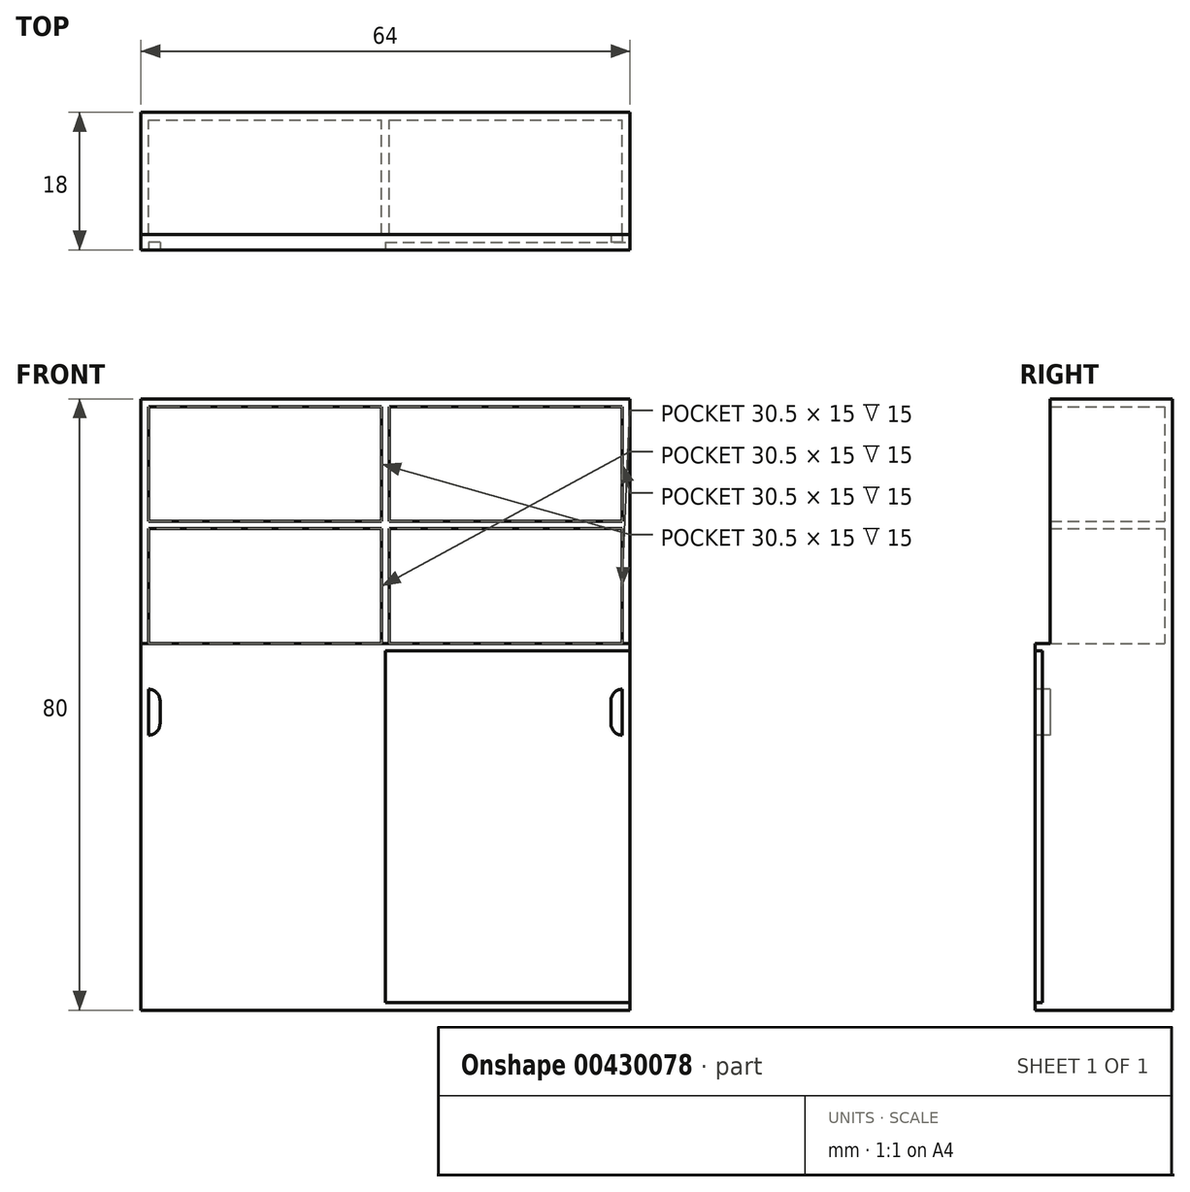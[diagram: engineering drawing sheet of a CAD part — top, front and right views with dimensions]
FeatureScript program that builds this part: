
annotation { "Feature Type Name" : "Feature", "Feature Type Description" : "" }
export const myFeature = defineFeature(function(context is Context, id is Id, definition is map)
    precondition{}
    {
        {
            var Q0;
            Q0=qCreatedBy(makeId("Top.planeOp"),FACE);
            var sketch = newSketch(context, id + "F0", { "sketchPlane" : qUnion([Q0])});
            skLineSegment(sketch, "E0.bottom", {"start": v(0, 0) * mm, "end": v(64, 0) * mm});
            skLineSegment(sketch, "E0.top", {"start": v(0, 18) * mm, "end": v(64, 18) * mm});
            skLineSegment(sketch, "E0.left", {"start": v(0, 0) * mm, "end": v(0, 18) * mm});
            skLineSegment(sketch, "E0.right", {"start": v(64, 0) * mm, "end": v(64, 18) * mm});
            skSolve(sketch);
        }
        {
            var Q0;
            Q0=makeQuery(id+"F0.imprint","IMPRINT",FACE,{"disambiguationData":[TD([[makeQuery(id+"F0.imprint","IMPRINT",EDGE,{"derivedFrom":sQuery(id+"F0.wireOp",EDGE,"E0.bottom")}),1.0]])]});
            extrude(context, id + "F1", {"entities" : qUnion([Q0]), "depth" : 48 * mm});
        }
        {
            var Q0;
            Q0=makeQuery(id+"F1.opExtrude","CAP_FACE",FACE,{"disambiguationData":[OSD([sQuery(id+"F0.wireOp",EDGE,"E0.bottom"),sQuery(id+"F0.wireOp",EDGE,"E0.top"),sQuery(id+"F0.wireOp",EDGE,"E0.left"),sQuery(id+"F0.wireOp",EDGE,"E0.right")])],"isStart":false});
            var sketch = newSketch(context, id + "F2", { "sketchPlane" : qUnion([Q0])});
            skLineSegment(sketch, "E1.bottom", {"start": v(0, 18) * mm, "end": v(64, 18) * mm});
            skLineSegment(sketch, "E1.top", {"start": v(0, 17) * mm, "end": v(64, 17) * mm});
            skLineSegment(sketch, "E1.left", {"start": v(0, 18) * mm, "end": v(0, 17) * mm});
            skLineSegment(sketch, "E1.right", {"start": v(64, 18) * mm, "end": v(64, 17) * mm});
            skSolve(sketch);
        }
        {
            var Q0;
            Q0=makeQuery(id+"F2.imprint","IMPRINT",FACE,{"disambiguationData":[TD([[makeQuery(id+"F2.imprint","IMPRINT",EDGE,{"derivedFrom":sQuery(id+"F2.wireOp",EDGE,"E1.bottom")}),-1.0]])]});
            extrude(context, id + "F3", {"entities" : qUnion([Q0]), "operationType" : NewBodyOperationType.ADD, "depth" : 32 * mm});
        }
        {
            var Q0;
            Q0=makeQuery(id+"F3.opExtrude","SWEPT_FACE",FACE,{"disambiguationData":[OSD([sQuery(id+"F2.wireOp",EDGE,"E1.top")])]});
            var sketch = newSketch(context, id + "F4", { "sketchPlane" : qUnion([Q0])});
            skLineSegment(sketch, "E2.bottom", {"start": v(0, 80) * mm, "end": v(1, 80) * mm});
            skLineSegment(sketch, "E2.top", {"start": v(0, 48) * mm, "end": v(1, 48) * mm});
            skLineSegment(sketch, "E2.left", {"start": v(0, 80) * mm, "end": v(0, 48) * mm});
            skLineSegment(sketch, "E2.right", {"start": v(1, 79) * mm, "end": v(1, 64) * mm});
            skLineSegment(sketch, "E3.bottom", {"start": v(63, 80) * mm, "end": v(64, 80) * mm});
            skLineSegment(sketch, "E3.top", {"start": v(63, 48) * mm, "end": v(64, 48) * mm});
            skLineSegment(sketch, "E3.left", {"start": v(63, 79) * mm, "end": v(63, 64) * mm});
            skLineSegment(sketch, "E3.right", {"start": v(64, 80) * mm, "end": v(64, 48) * mm});
            skLineSegment(sketch, "E4.bottom", {"start": v(31.5, 80) * mm, "end": v(32.5, 80) * mm});
            skLineSegment(sketch, "E4.top", {"start": v(31.5, 48) * mm, "end": v(32.5, 48) * mm});
            skLineSegment(sketch, "E4.left", {"start": v(31.5, 79) * mm, "end": v(31.5, 64) * mm});
            skLineSegment(sketch, "E4.right", {"start": v(32.5, 79) * mm, "end": v(32.5, 64) * mm});
            skLineSegment(sketch, "E5.bottom", {"start": v(0, 80) * mm, "end": v(64, 80) * mm});
            skLineSegment(sketch, "E5.top", {"start": v(1, 79) * mm, "end": v(31.5, 79) * mm});
            skLineSegment(sketch, "E5.left", {"start": v(0, 80) * mm, "end": v(0, 79) * mm});
            skLineSegment(sketch, "E5.right", {"start": v(64, 80) * mm, "end": v(64, 79) * mm});
            skLineSegment(sketch, "E6.bottom", {"start": v(1, 64) * mm, "end": v(31.5, 64) * mm});
            skLineSegment(sketch, "E6.top", {"start": v(1, 63) * mm, "end": v(31.5, 63) * mm});
            skLineSegment(sketch, "E6.left", {"start": v(0, 64) * mm, "end": v(0, 63) * mm});
            skLineSegment(sketch, "E6.right", {"start": v(64, 64) * mm, "end": v(64, 64) * mm});
            skLineSegment(sketch, "E7.trimOffspring", {"start": v(32.5, 79) * mm, "end": v(63, 79) * mm});
            skLineSegment(sketch, "E8.trimOffspring", {"start": v(1, 63) * mm, "end": v(1, 48) * mm});
            skLineSegment(sketch, "E9.trimOffspring", {"start": v(32.5, 64) * mm, "end": v(63, 64) * mm});
            skLineSegment(sketch, "E10.trimOffspring", {"start": v(32.5, 63) * mm, "end": v(32.5, 48) * mm});
            skLineSegment(sketch, "E11.trimOffspring", {"start": v(31.5, 63) * mm, "end": v(31.5, 48) * mm});
            skLineSegment(sketch, "E12.trimOffspring", {"start": v(63, 63) * mm, "end": v(63, 48) * mm});
            skLineSegment(sketch, "E13.trimOffspring", {"start": v(32.5, 63) * mm, "end": v(63, 63) * mm});
            skSolve(sketch);
        }
        {
            var Q0;
            Q0 = qSketchRegion(id + "F4", true);
            extrude(context, id + "F5", {"entities" : qUnion([Q0]), "operationType" : NewBodyOperationType.ADD, "depth" : 15 * mm});
        }
        {
            var Q0;
            Q0=makeQuery(id+"F1.opExtrude","SWEPT_FACE",FACE,{"disambiguationData":[OSD([sQuery(id+"F0.wireOp",EDGE,"E0.bottom")])]});
            var sketch = newSketch(context, id + "F6", { "sketchPlane" : qUnion([Q0])});
            skLineSegment(sketch, "E14.bottom", {"start": v(32, 47) * mm, "end": v(64, 47) * mm});
            skLineSegment(sketch, "E14.top", {"start": v(32, 1) * mm, "end": v(64, 1) * mm});
            skLineSegment(sketch, "E14.left", {"start": v(32, 47) * mm, "end": v(32, 1) * mm});
            skLineSegment(sketch, "E14.right", {"start": v(64, 47) * mm, "end": v(64, 1) * mm});
            skSolve(sketch);
        }
        {
            var Q0;
            Q0=makeQuery(id+"F6.imprint","IMPRINT",FACE,{"disambiguationData":[TD([[makeQuery(id+"F6.imprint","IMPRINT",EDGE,{"derivedFrom":sQuery(id+"F6.wireOp",EDGE,"E14.bottom")}),-1.0]])]});
            extrude(context, id + "F7", {"entities" : qUnion([Q0]), "operationType" : NewBodyOperationType.REMOVE, "oppositeDirection" : true, "depth" : 1 * mm});
        }
        {
            var Q0;
            Q0=makeQuery(id+"F7.boolean.opBoolean","COPY",FACE,{"derivedFrom":makeQuery(id+"F7.opExtrude","CAP_FACE",FACE,{"disambiguationData":[OSD([sQuery(id+"F6.wireOp",EDGE,"E14.bottom"),sQuery(id+"F6.wireOp",EDGE,"E14.top"),sQuery(id+"F6.wireOp",EDGE,"E14.left"),sQuery(id+"F6.wireOp",EDGE,"E14.right")])],"isStart":false})});
            var sketch = newSketch(context, id + "F8", { "sketchPlane" : qUnion([Q0])});
            skLineSegment(sketch, "E15.bottom", {"start": v(63, 42) * mm, "end": v(63, 42) * mm});
            skLineSegment(sketch, "E15.top", {"start": v(63, 36) * mm, "end": v(63, 36) * mm});
            skLineSegment(sketch, "E15.left", {"start": v(61.5, 40.5) * mm, "end": v(61.5, 37.5) * mm});
            skLineSegment(sketch, "E16", {"start": v(63, 42) * mm, "end": v(63, 36) * mm});
            skPoint(sketch, "E17.visualSharp", {"position": v(61.5, 42) * mm});
            skArc(sketch, "E17.filletArc", {"start": v(63, 42) * mm, "mid": v(61.94, 41.56) * mm, "end": v(61.5, 40.5) * mm});
            skPoint(sketch, "E18.visualSharp", {"position": v(61.5, 36) * mm});
            skArc(sketch, "E18.filletArc", {"start": v(61.5, 37.5) * mm, "mid": v(61.94, 36.44) * mm, "end": v(63, 36) * mm});
            skSolve(sketch);
        }
        {
            var Q0;
            Q0=makeQuery(id+"F8.imprint","IMPRINT",FACE,{"disambiguationData":[TD([[makeQuery(id+"F8.imprint","IMPRINT",EDGE,{"derivedFrom":sQuery(id+"F8.wireOp",EDGE,"E15.left")}),1.0]])]});
            extrude(context, id + "F9", {"entities" : qUnion([Q0]), "operationType" : NewBodyOperationType.REMOVE, "oppositeDirection" : true, "depth" : 1 * mm});
        }
        {
            var Q0;
            Q0=makeQuery(id+"F1.opExtrude","SWEPT_FACE",FACE,{"disambiguationData":[OSD([sQuery(id+"F0.wireOp",EDGE,"E0.bottom")])]});
            var sketch = newSketch(context, id + "F10", { "sketchPlane" : qUnion([Q0])});
            skLineSegment(sketch, "E19.bottom", {"start": v(1, 42) * mm, "end": v(1, 42) * mm});
            skLineSegment(sketch, "E19.top", {"start": v(1, 36) * mm, "end": v(1, 36) * mm});
            skLineSegment(sketch, "E19.left", {"start": v(1, 42) * mm, "end": v(1, 36) * mm});
            skLineSegment(sketch, "E19.right", {"start": v(2.5, 40.5) * mm, "end": v(2.5, 37.5) * mm});
            skPoint(sketch, "E20.visualSharp", {"position": v(2.5, 42) * mm});
            skArc(sketch, "E20.filletArc", {"start": v(2.5, 40.5) * mm, "mid": v(2.06, 41.56) * mm, "end": v(1, 42) * mm});
            skPoint(sketch, "E21.visualSharp", {"position": v(2.5, 36) * mm});
            skArc(sketch, "E21.filletArc", {"start": v(1, 36) * mm, "mid": v(2.06, 36.44) * mm, "end": v(2.5, 37.5) * mm});
            skSolve(sketch);
        }
        {
            var Q0;
            Q0=makeQuery(id+"F10.imprint","IMPRINT",FACE,{"disambiguationData":[TD([[makeQuery(id+"F10.imprint","IMPRINT",EDGE,{"derivedFrom":sQuery(id+"F10.wireOp",EDGE,"E19.left")}),1.0]])]});
            extrude(context, id + "F11", {"entities" : qUnion([Q0]), "operationType" : NewBodyOperationType.REMOVE, "oppositeDirection" : true, "depth" : 1 * mm});
        }
    });
